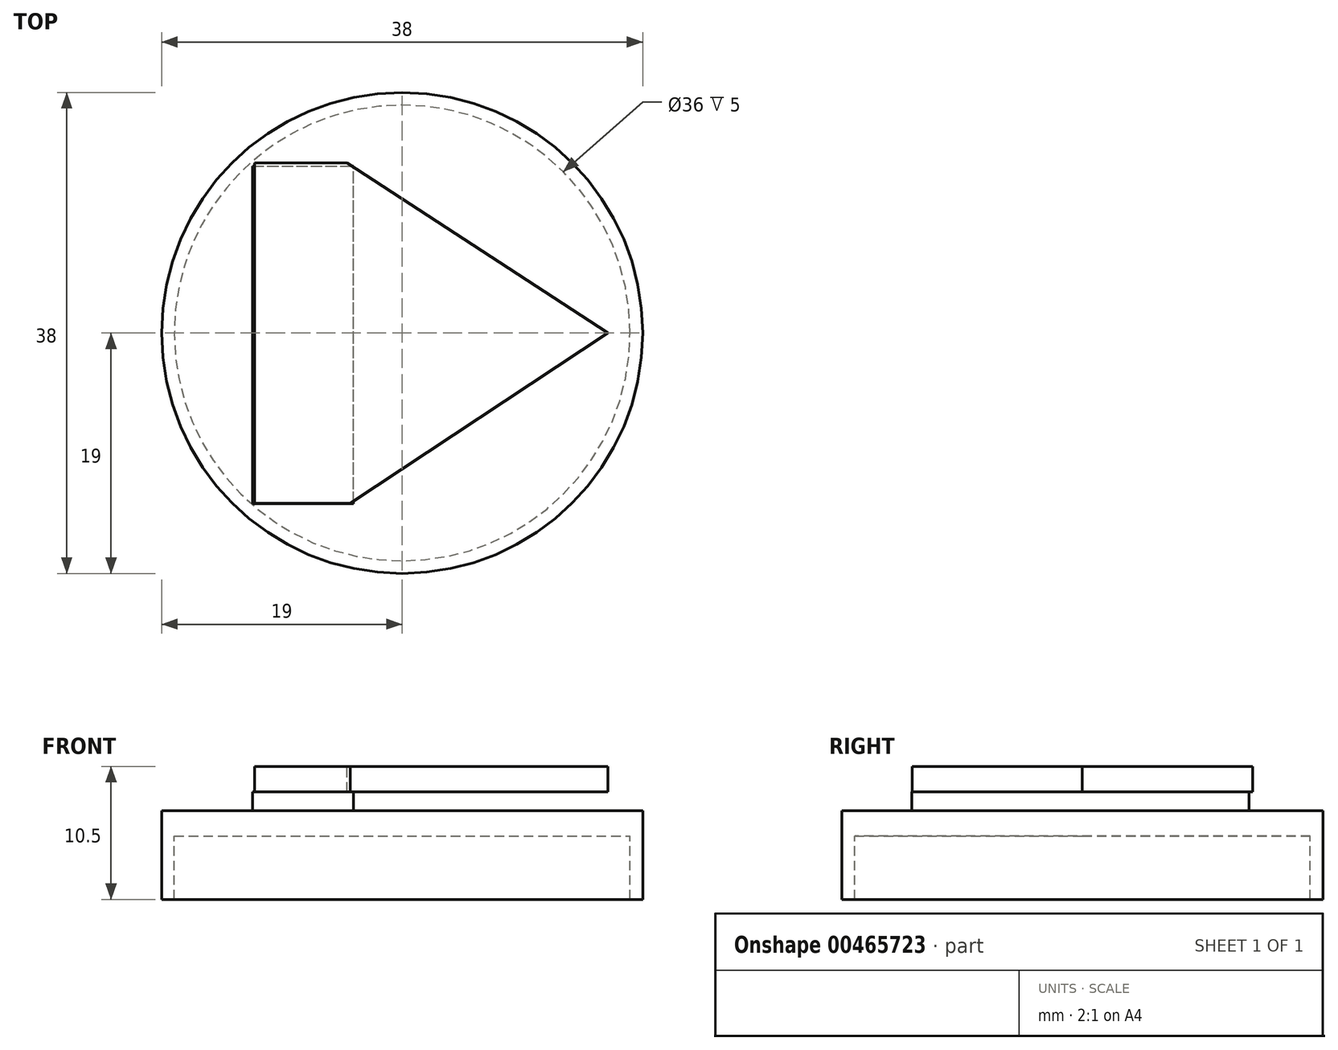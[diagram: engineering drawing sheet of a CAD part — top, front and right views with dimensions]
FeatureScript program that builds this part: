
annotation { "Feature Type Name" : "Feature", "Feature Type Description" : "" }
export const myFeature = defineFeature(function(context is Context, id is Id, definition is map)
    precondition{}
    {
        {
            var Q0;
            Q0=qCreatedBy(makeId("Top.planeOp"),FACE);
            var sketch = newSketch(context, id + "F0", { "sketchPlane" : qUnion([Q0])});
            skCircle(sketch, "E0", {"center": v(0, 0) * mm, "radius": 19 * mm});
            skSolve(sketch);
        }
        {
            var Q0;
            Q0=makeQuery(id+"F0.imprint","IMPRINT",FACE,{"disambiguationData":[TD([[makeQuery(id+"F0.imprint","IMPRINT",EDGE,{"derivedFrom":sQuery(id+"F0.wireOp",EDGE,"E0")}),1.0]])]});
            extrude(context, id + "F1", {"entities" : qUnion([Q0]), "depth" : 2 * mm});
        }
        {
            var Q0;
            Q0=makeQuery(id+"F1.opExtrude","CAP_FACE",FACE,{"disambiguationData":[OSD([sQuery(id+"F0.wireOp",EDGE,"E0")])],"isStart":false});
            var sketch = newSketch(context, id + "F2", { "sketchPlane" : qUnion([Q0])});
            skLineSegment(sketch, "E1.bottom", {"start": v(-11.8, -13.49) * mm, "end": v(-3.84, -13.49) * mm});
            skLineSegment(sketch, "E1.top", {"start": v(-11.8, 13.18) * mm, "end": v(-3.84, 13.18) * mm});
            skLineSegment(sketch, "E1.left", {"start": v(-11.8, -13.49) * mm, "end": v(-11.8, 13.18) * mm});
            skLineSegment(sketch, "E1.right", {"start": v(-3.84, -13.49) * mm, "end": v(-3.84, 13.18) * mm});
            skSolve(sketch);
        }
        {
            var Q0;
            Q0 = qSketchRegion(id + "F2", true);
            extrude(context, id + "F3", {"entities" : qUnion([Q0]), "operationType" : NewBodyOperationType.ADD, "depth" : .75 * mm});
        }
        {
            var Q0;
            Q0=makeQuery(id+"F1.opExtrude","SWEPT_BODY",BODY,{"disambiguationData":[OSD([sQuery(id+"F0.wireOp",EDGE,"E0")])]});
            var Q1;
            Q1=makeQuery(id+"F3.opExtrude","CAP_FACE",FACE,{"disambiguationData":[OSD([sQuery(id+"F2.wireOp",EDGE,"E1.bottom"),sQuery(id+"F2.wireOp",EDGE,"E1.top"),sQuery(id+"F2.wireOp",EDGE,"E1.left"),sQuery(id+"F2.wireOp",EDGE,"E1.right")])],"isStart":false});
            mirror(context, id + "F4", {"operationType" : NewBodyOperationType.ADD, "entities" : qUnion([Q0]), "mirrorPlane" : qUnion([Q1])});
        }
        {
            var Q0;
            Q0=makeQuery(id+"F4.opPattern","COPY",FACE,{"derivedFrom":makeQuery(id+"F1.opExtrude","CAP_FACE",FACE,{"disambiguationData":[OSD([sQuery(id+"F0.wireOp",EDGE,"E0")])],"isStart":true}),"instanceName":"1"});
            var sketch = newSketch(context, id + "F5", { "sketchPlane" : qUnion([Q0])});
            skLineSegment(sketch, "E2", {"start": v(16.25, 0) * mm, "end": v(-4.36, 13.45) * mm});
            skLineSegment(sketch, "E3", {"start": v(-4.36, 13.45) * mm, "end": v(-11.66, 13.45) * mm});
            skLineSegment(sketch, "E4", {"start": v(-11.66, 13.45) * mm, "end": v(-11.66, -13.45) * mm});
            skLineSegment(sketch, "E5", {"start": v(-11.66, -13.45) * mm, "end": v(-4.09, -13.45) * mm});
            skLineSegment(sketch, "E6", {"start": v(-4.09, -13.45) * mm, "end": v(16.25, 0) * mm});
            skSolve(sketch);
        }
        {
            var Q0;
            Q0=makeQuery(id+"F5.imprint","IMPRINT",FACE,{"disambiguationData":[TD([[makeQuery(id+"F5.imprint","IMPRINT",EDGE,{"derivedFrom":sQuery(id+"F5.wireOp",EDGE,"E2")}),-1.0]])]});
            extrude(context, id + "F6", {"entities" : qUnion([Q0]), "operationType" : NewBodyOperationType.REMOVE, "oppositeDirection" : true, "depth" : 2 * mm});
        }
        {
            var Q0;
            Q0=makeQuery(id+"F1.opExtrude","CAP_FACE",FACE,{"disambiguationData":[OSD([sQuery(id+"F0.wireOp",EDGE,"E0")])],"isStart":true});
            var sketch = newSketch(context, id + "F7", { "sketchPlane" : qUnion([Q0])});
            skCircle(sketch, "E7", {"center": v(0, 0) * mm, "radius": 18 * mm});
            skSolve(sketch);
        }
        {
            var Q0;
            Q0=makeQuery(id+"F7.imprint","IMPRINT",FACE,{"disambiguationData":[TD([[makeQuery(id+"F7.imprint","IMPRINT",EDGE,{"derivedFrom":sQuery(id+"F7.wireOp",EDGE,"E7")}),-1.0]])]});
            extrude(context, id + "F8", {"entities" : qUnion([Q0]), "operationType" : NewBodyOperationType.ADD, "depth" : 5 * mm});
        }
    });
